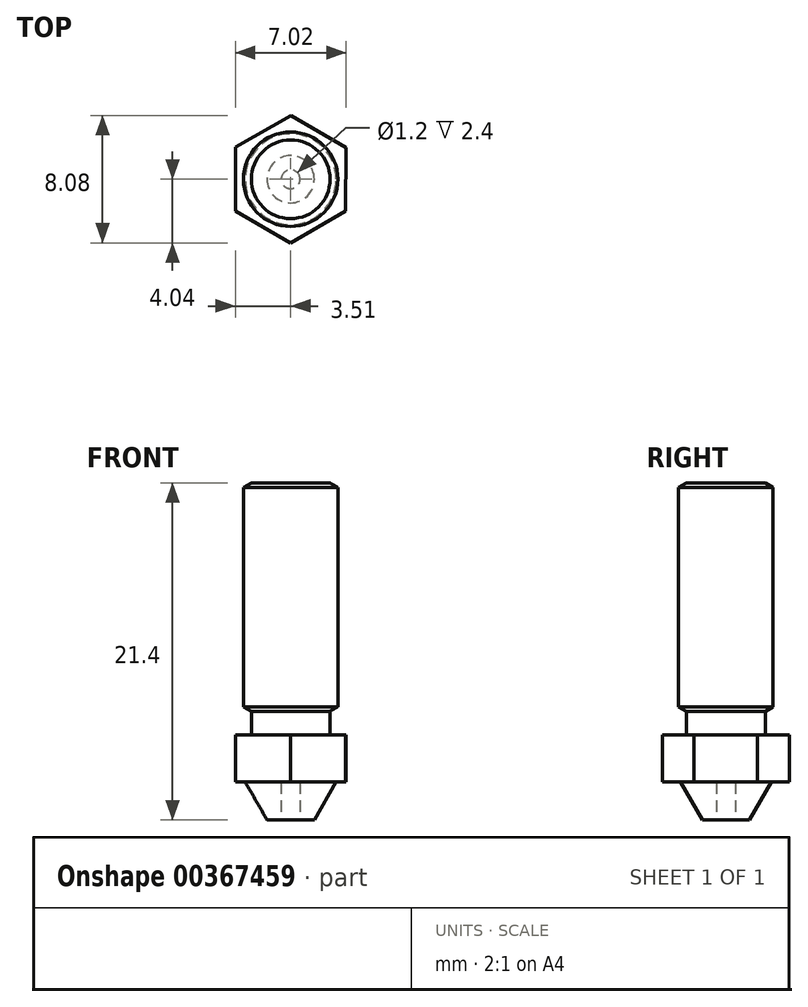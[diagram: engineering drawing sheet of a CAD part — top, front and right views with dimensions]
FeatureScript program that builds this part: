
annotation { "Feature Type Name" : "Feature", "Feature Type Description" : "" }
export const myFeature = defineFeature(function(context is Context, id is Id, definition is map)
    precondition{}
    {
        {
            var Q0;
            Q0=qCreatedBy(makeId("Front.planeOp"),FACE);
            var sketch = newSketch(context, id + "F0", { "sketchPlane" : qUnion([Q0])});
            skLineSegment(sketch, "E0", {"start": v(0, 0) * mm, "end": v(0.9, 0) * mm});
            skLineSegment(sketch, "E1", {"start": v(0.9, 0) * mm, "end": v(2.29, 2.4) * mm});
            skLineSegment(sketch, "E2", {"start": v(2.29, 2.4) * mm, "end": v(0, 2.4) * mm});
            skLineSegment(sketch, "E3", {"start": v(-0.6, 0) * mm, "end": v(-0.6, 2.4) * mm, "construction": true});
            skLineSegment(sketch, "E4", {"start": v(0, 0) * mm, "end": v(0, 2.4) * mm});
            skSolve(sketch);
        }
        {
            var Q0;
            Q0=qSketchRegion(id+"F0",true);
            var Q1;
            Q1=sQuery(id+"F0.wireOp",EDGE,"E3");
            revolve(context, id + "F1", {"entities" : qUnion([Q0]), "axis" : qUnion([Q1]), "revolveType" : RevolveType.FULL});
        }
        {
            var Q0;
            Q0=makeQuery(id+"F1.opRevolve","SWEPT_FACE",FACE,{"disambiguationData":[OSD([sQuery(id+"F0.wireOp",EDGE,"E2")])]});
            var sketch = newSketch(context, id + "F2", { "sketchPlane" : qUnion([Q0])});
            skCircle(sketch, "E5.cCircle", {"center": v(-0.6, 0) * mm, "radius": 3.5 * mm, "construction": true});
            skLineSegment(sketch, "E5.0", {"start": v(-0.59, 4.04) * mm, "end": v(2.9, 2) * mm});
            skLineSegment(sketch, "E5.1", {"start": v(2.9, 2) * mm, "end": v(2.9, -2.03) * mm});
            skLineSegment(sketch, "E5.2", {"start": v(2.9, -2.03) * mm, "end": v(-0.61, -4.04) * mm});
            skLineSegment(sketch, "E5.3", {"start": v(-0.61, -4.04) * mm, "end": v(-4.1, -2) * mm});
            skLineSegment(sketch, "E5.4", {"start": v(-4.1, -2) * mm, "end": v(-4.1, 2.03) * mm});
            skLineSegment(sketch, "E5.5", {"start": v(-4.1, 2.03) * mm, "end": v(-0.59, 4.04) * mm});
            skPoint(sketch, "E5.0.midPoint", {"position": v(1.16, 3.02) * mm});
            skSolve(sketch);
        }
        {
            var Q0;
            Q0=qSketchRegion(id+"F2",true);
            extrude(context, id + "F3", {"entities" : qUnion([Q0]), "operationType" : NewBodyOperationType.ADD, "depth" : 3 * mm});
        }
        {
            var Q0;
            Q0=makeQuery(id+"F3.opExtrude","CAP_FACE",FACE,{"disambiguationData":[OSD([sQuery(id+"F2.wireOp",EDGE,"E5.0"),sQuery(id+"F2.wireOp",EDGE,"E5.1"),sQuery(id+"F2.wireOp",EDGE,"E5.2"),sQuery(id+"F2.wireOp",EDGE,"E5.3"),sQuery(id+"F2.wireOp",EDGE,"E5.4"),sQuery(id+"F2.wireOp",EDGE,"E5.5")])],"isStart":false});
            var sketch = newSketch(context, id + "F4", { "sketchPlane" : qUnion([Q0])});
            skCircle(sketch, "E6", {"center": v(-0.6, 0) * mm, "radius": 2.5 * mm});
            skSolve(sketch);
        }
        {
            var Q0;
            Q0=qSketchRegion(id+"F4",true);
            extrude(context, id + "F5", {"entities" : qUnion([Q0]), "operationType" : NewBodyOperationType.ADD, "depth" : 1.5 * mm});
        }
        {
            var Q0;
            Q0=makeQuery(id+"F5.opExtrude","CAP_FACE",FACE,{"disambiguationData":[OSD([sQuery(id+"F4.wireOp",EDGE,"E6")])],"isStart":false});
            var sketch = newSketch(context, id + "F6", { "sketchPlane" : qUnion([Q0])});
            skCircle(sketch, "E7", {"center": v(-0.6, 0) * mm, "radius": 3 * mm});
            skSolve(sketch);
        }
        {
            var Q0;
            Q0=qSketchRegion(id+"F6",true);
            extrude(context, id + "F7", {"entities" : qUnion([Q0]), "operationType" : NewBodyOperationType.ADD, "depth" : 14.5 * mm});
        }
        {
            var Q0;
            Q0=makeQuery(id+"F7.opExtrude","CAP_EDGE",EDGE,{"disambiguationData":[OSD([sQuery(id+"F6.wireOp",EDGE,"E7")])],"isStart":false});
            var Q1;
            Q1=makeQuery(id+"F7.opExtrude","CAP_EDGE",EDGE,{"disambiguationData":[OSD([sQuery(id+"F6.wireOp",EDGE,"E7")])],"isStart":true});
            chamfer(context, id + "F8", {"entities" : qUnion([Q0, Q1]), "chamferType" : ChamferType.OFFSET_ANGLE, "width" : 0.5 * mm, "oppositeDirection" : false, "angle" : 30 * degree, "tangentPropagation" : true});
        }
    });
